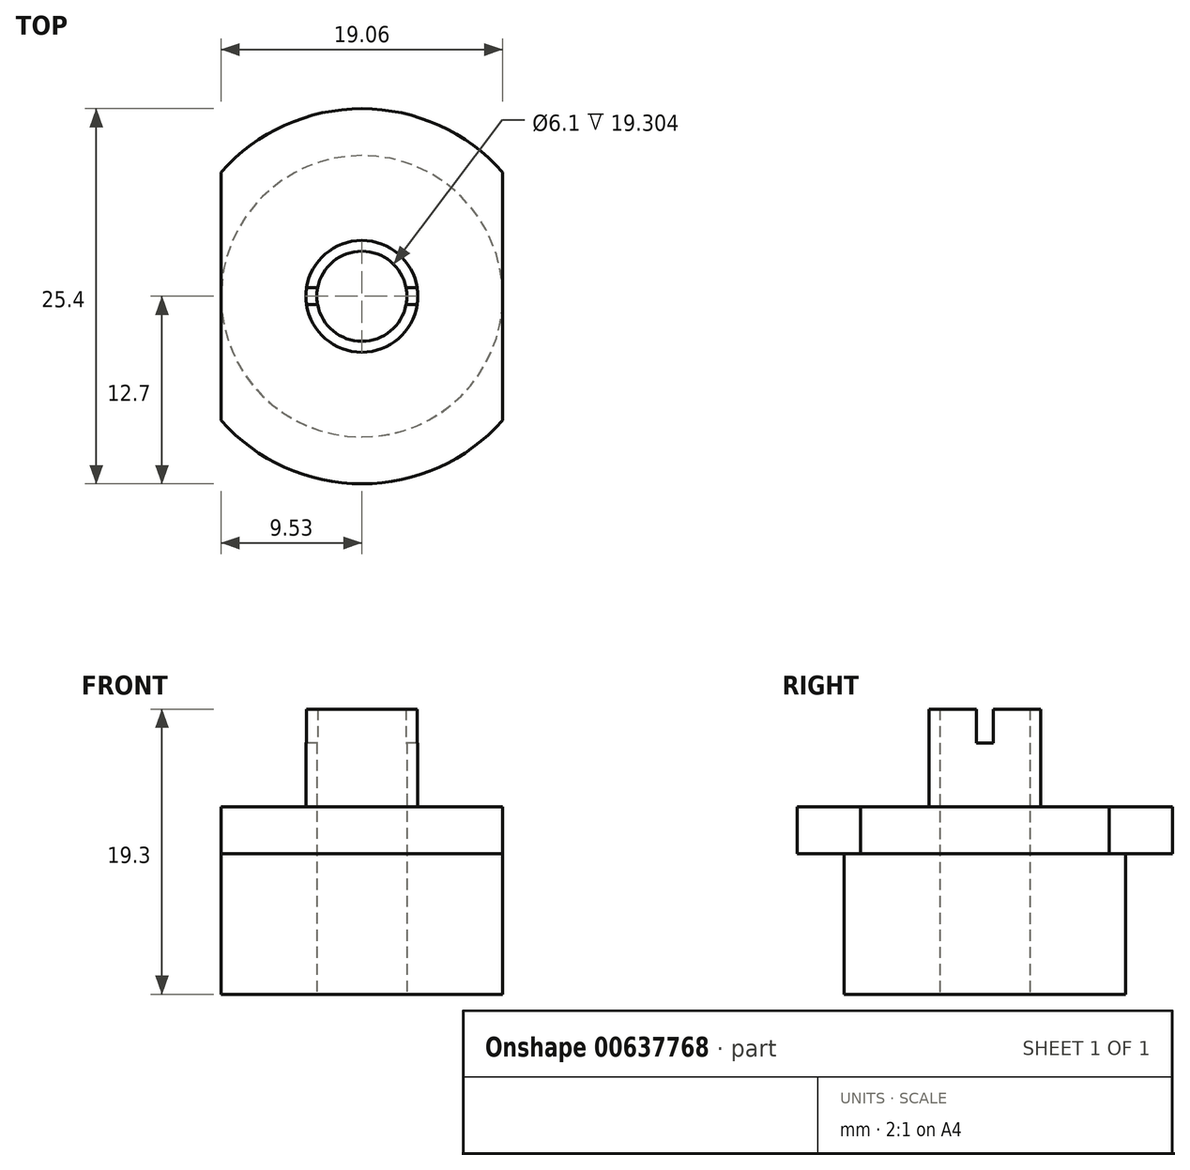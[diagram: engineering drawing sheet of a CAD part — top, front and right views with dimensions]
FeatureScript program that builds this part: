
annotation { "Feature Type Name" : "Feature", "Feature Type Description" : "" }
export const myFeature = defineFeature(function(context is Context, id is Id, definition is map)
    precondition{}
    {
        {
            var Q0;
            Q0=qCreatedBy(makeId("Top.planeOp"),FACE);
            var sketch = newSketch(context, id + "F0", { "sketchPlane" : qUnion([Q0])});
            skCircle(sketch, "E0", {"center": v(0, 0) * mm, "radius": 9.53 * mm});
            skSolve(sketch);
        }
        {
            var Q0;
            Q0=makeQuery(id+"F0.imprint","IMPRINT",FACE,{"disambiguationData":[TD([[makeQuery(id+"F0.imprint","IMPRINT",EDGE,{"derivedFrom":sQuery(id+"F0.wireOp",EDGE,"E0")}),1.0]])]});
            extrude(context, id + "F1", {"entities" : qUnion([Q0]), "depth" : 9.52 * mm, "offsetDistance" : 25.4 * mm});
        }
        {
            var Q0;
            Q0=makeQuery(id+"F1.opExtrude","CAP_FACE",FACE,{"disambiguationData":[OSD([sQuery(id+"F0.wireOp",EDGE,"E0")])],"isStart":false});
            var sketch = newSketch(context, id + "F2", { "sketchPlane" : qUnion([Q0])});
            skCircle(sketch, "E1", {"center": v(0, 0) * mm, "radius": 12.7 * mm});
            skSolve(sketch);
        }
        {
            var Q0;
            Q0=makeQuery(id+"F2.imprint","IMPRINT",FACE,{"disambiguationData":[TD([[makeQuery(id+"F2.imprint","IMPRINT",EDGE,{"derivedFrom":sQuery(id+"F2.wireOp",EDGE,"E1")}),1.0]])]});
            var Q1;
            Q1=makeQuery(id+"F2.imprint","IMPRINT",FACE,{"disambiguationData":[TD([[makeQuery(id+"F2.imprint","IMPRINT",EDGE,{"derivedFrom":makeQuery(id+"F1.opExtrude","CAP_EDGE",EDGE,{"disambiguationData":[OSD([sQuery(id+"F0.wireOp",EDGE,"E0")])],"isStart":false})}),1.0]])]});
            extrude(context, id + "F3", {"entities" : qUnion([Q0, Q1]), "operationType" : NewBodyOperationType.ADD, "depth" : 3.17 * mm, "offsetDistance" : 25.4 * mm});
        }
        {
            var Q0;
            Q0=makeQuery(id+"F3.opExtrude","CAP_FACE",FACE,{"disambiguationData":[OSD([sQuery(id+"F2.wireOp",EDGE,"E1")])],"isStart":false});
            var sketch = newSketch(context, id + "F4", { "sketchPlane" : qUnion([Q0])});
            skLineSegment(sketch, "E2", {"start": v(-9.53, -8.4) * mm, "end": v(-9.53, 8.4) * mm});
            skLineSegment(sketch, "E3", {"start": v(9.53, -8.4) * mm, "end": v(9.53, 8.4) * mm});
            skLineSegment(sketch, "E4", {"start": v(9.53, -8.4) * mm, "end": v(23.26, -8.4) * mm});
            skLineSegment(sketch, "E5", {"start": v(23.26, -8.4) * mm, "end": v(23.26, 8.64) * mm});
            skLineSegment(sketch, "E6", {"start": v(23.26, 8.64) * mm, "end": v(9.53, 8.4) * mm});
            skLineSegment(sketch, "E7", {"start": v(-9.53, -8.4) * mm, "end": v(-22.83, -8.4) * mm});
            skLineSegment(sketch, "E8", {"start": v(-22.83, -8.4) * mm, "end": v(-22.83, 8.4) * mm});
            skLineSegment(sketch, "E9", {"start": v(-22.83, 8.4) * mm, "end": v(-9.53, 8.4) * mm});
            skSolve(sketch);
        }
        {
            var Q0;
            {var subQ0=sQuery(id+"F4.wireOp",EDGE,"E2");Q0=makeQuery(id+"F4.imprint","IMPRINT",FACE,{"disambiguationData":[TD([[makeQuery(id+"F4.imprint","IMPRINT",EDGE,{"derivedFrom":subQ0}),1.0]])]});}
            var Q1;
            {var subQ0=sQuery(id+"F4.wireOp",EDGE,"E3");Q1=makeQuery(id+"F4.imprint","IMPRINT",FACE,{"disambiguationData":[TD([[makeQuery(id+"F4.imprint","IMPRINT",EDGE,{"derivedFrom":subQ0}),-1.0]])]});}
            extrude(context, id + "F5", {"entities" : qUnion([Q0, Q1]), "operationType" : NewBodyOperationType.REMOVE, "oppositeDirection" : true, "depth" : 25.4 * mm, "offsetDistance" : 25.4 * mm});
        }
        {
            var Q0;
            Q0=makeQuery(id+"F3.opExtrude","CAP_FACE",FACE,{"disambiguationData":[OSD([sQuery(id+"F2.wireOp",EDGE,"E1")])],"isStart":false});
            var sketch = newSketch(context, id + "F6", { "sketchPlane" : qUnion([Q0])});
            skCircle(sketch, "E10", {"center": v(0, 0) * mm, "radius": 3.05 * mm});
            skCircle(sketch, "E11", {"center": v(0, 0) * mm, "radius": 3.78 * mm});
            skSolve(sketch);
        }
        {
            var Q0;
            Q0=makeQuery(id+"F6.imprint","IMPRINT",FACE,{"disambiguationData":[TD([[makeQuery(id+"F6.imprint","IMPRINT",EDGE,{"derivedFrom":sQuery(id+"F6.wireOp",EDGE,"E10")}),-1.0]])]});
            extrude(context, id + "F7", {"entities" : qUnion([Q0]), "operationType" : NewBodyOperationType.ADD, "depth" : 6.6 * mm, "offsetDistance" : 25.4 * mm});
        }
        {
            var Q0;
            Q0=makeQuery(id+"F7.boolean.opBoolean","SPLIT",FACE,{"disambiguationData":[TD([makeQuery(id+"F7.opExtrude","SWEPT_FACE",FACE,{"disambiguationData":[OSD([sQuery(id+"F6.wireOp",EDGE,"E10")])]})])],"derivedFrom":makeQuery(id+"F3.opExtrude","CAP_FACE",FACE,{"disambiguationData":[OSD([sQuery(id+"F2.wireOp",EDGE,"E1")])],"isStart":false})});
            extrude(context, id + "F8", {"entities" : qUnion([Q0]), "operationType" : NewBodyOperationType.REMOVE, "endBound" : BoundingType.THROUGH_ALL, "oppositeDirection" : true, "depth" : 25.4 * mm, "offsetDistance" : 25.4 * mm});
        }
        {
            var Q0;
            Q0=makeQuery(id+"F7.opExtrude","CAP_FACE",FACE,{"disambiguationData":[OSD([sQuery(id+"F6.wireOp",EDGE,"E10"),sQuery(id+"F6.wireOp",EDGE,"E11")])],"isStart":false});
            var sketch = newSketch(context, id + "F9", { "sketchPlane" : qUnion([Q0])});
            skLineSegment(sketch, "E12.bottom", {"start": v(4.08, -0.57) * mm, "end": v(-4.08, -0.57) * mm});
            skLineSegment(sketch, "E12.top", {"start": v(4.08, 0.57) * mm, "end": v(-4.08, 0.57) * mm});
            skLineSegment(sketch, "E12.left", {"start": v(4.08, -0.57) * mm, "end": v(4.08, 0.57) * mm});
            skLineSegment(sketch, "E12.right", {"start": v(-4.08, -0.57) * mm, "end": v(-4.08, 0.57) * mm});
            skPoint(sketch, "E12.middle", {"position": v(0, 0) * mm});
            skSolve(sketch);
        }
        {
            var Q0;
            {var subQ0=sQuery(id+"F9.wireOp",EDGE,"E12.left");Q0=makeQuery(id+"F9.imprint","IMPRINT",FACE,{"disambiguationData":[TD([[makeQuery(id+"F9.imprint","IMPRINT",EDGE,{"derivedFrom":subQ0}),1.0]])]});}
            var Q1;
            {var subQ0=sQuery(id+"F9.wireOp",EDGE,"E12.right");Q1=makeQuery(id+"F9.imprint","IMPRINT",FACE,{"disambiguationData":[TD([[makeQuery(id+"F9.imprint","IMPRINT",EDGE,{"derivedFrom":subQ0}),-1.0]])]});}
            var Q2;
            {var subQ0=sQuery(id+"F9.wireOp",EDGE,"E12.bottom");var subQ1=makeQuery(id+"F7.opExtrude","CAP_EDGE",EDGE,{"disambiguationData":[OSD([sQuery(id+"F6.wireOp",EDGE,"E11")])],"isStart":false});var subQ2=makeQuery(id+"F9.imprint","INTERSECT",VERTEX,{"disambiguationData":[OD(0.0)],"derivedFrom":[subQ1,subQ0]});Q2=makeQuery(id+"F9.imprint","IMPRINT",FACE,{"disambiguationData":[TD([[makeQuery(id+"F9.imprint","IMPRINT",EDGE,{"disambiguationData":[TD([[subQ2,-1.0]])],"derivedFrom":subQ0}),-1.0]])]});}
            var Q3;
            {var subQ0=sQuery(id+"F9.wireOp",EDGE,"E12.bottom");var subQ1=makeQuery(id+"F7.opExtrude","CAP_EDGE",EDGE,{"disambiguationData":[OSD([sQuery(id+"F6.wireOp",EDGE,"E11")])],"isStart":false});var subQ2=makeQuery(id+"F9.imprint","INTERSECT",VERTEX,{"disambiguationData":[OD(1.0)],"derivedFrom":[subQ1,subQ0]});Q3=makeQuery(id+"F9.imprint","IMPRINT",FACE,{"disambiguationData":[TD([[makeQuery(id+"F9.imprint","IMPRINT",EDGE,{"disambiguationData":[TD([[subQ2,1.0]])],"derivedFrom":subQ0}),-1.0]])]});}
            var Q4;
            {var subQ0=sQuery(id+"F9.wireOp",EDGE,"E12.bottom");var subQ1=makeQuery(id+"F7.opExtrude","CAP_EDGE",EDGE,{"disambiguationData":[OSD([sQuery(id+"F6.wireOp",EDGE,"E10")])],"isStart":false});var subQ2=makeQuery(id+"F9.imprint","INTERSECT",VERTEX,{"disambiguationData":[OD(0.0)],"derivedFrom":[subQ1,subQ0]});Q4=makeQuery(id+"F9.imprint","IMPRINT",FACE,{"disambiguationData":[TD([[makeQuery(id+"F9.imprint","IMPRINT",EDGE,{"disambiguationData":[TD([[subQ2,-1.0]])],"derivedFrom":subQ0}),-1.0]])]});}
            extrude(context, id + "F10", {"entities" : qUnion([Q0, Q1, Q2, Q3, Q4]), "operationType" : NewBodyOperationType.REMOVE, "oppositeDirection" : true, "depth" : 2.3 * mm, "offsetDistance" : 25.4 * mm});
        }
    });
